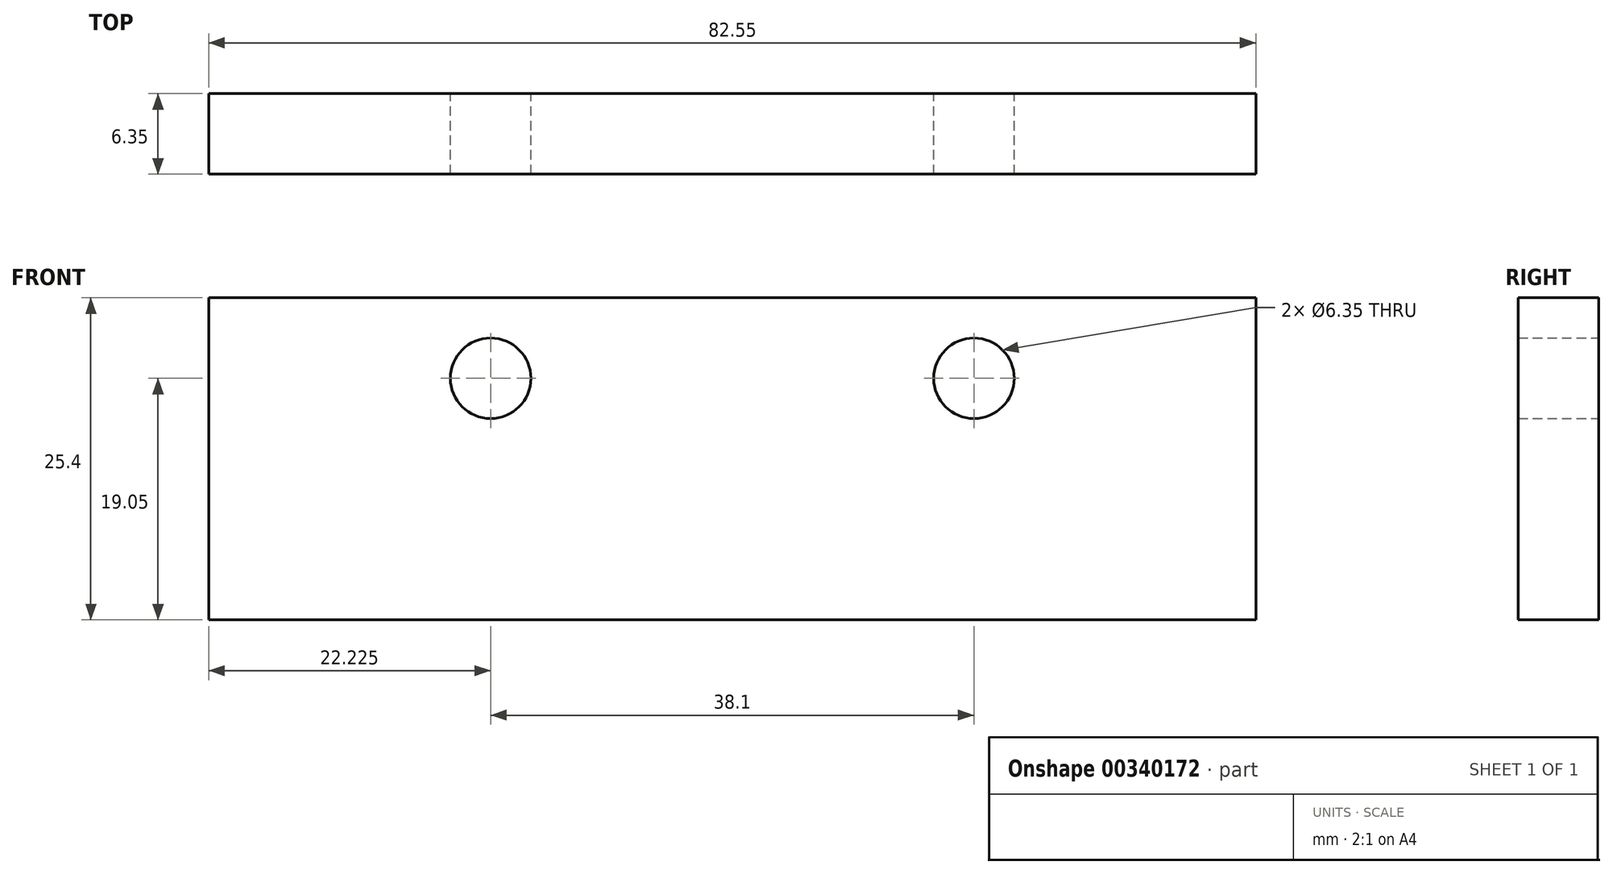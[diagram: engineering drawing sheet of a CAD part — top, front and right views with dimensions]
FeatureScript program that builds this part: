
annotation { "Feature Type Name" : "Feature", "Feature Type Description" : "" }
export const myFeature = defineFeature(function(context is Context, id is Id, definition is map)
    precondition{}
    {
        {
            var Q0;
            Q0=qCreatedBy(makeId("Front.planeOp"),FACE);
            var sketch = newSketch(context, id + "F0", { "sketchPlane" : qUnion([Q0])});
            skLineSegment(sketch, "E0.bottom", {"start": v(0, 0) * mm, "end": v(82.55, 0) * mm});
            skLineSegment(sketch, "E0.top", {"start": v(0, 25.4) * mm, "end": v(82.55, 25.4) * mm});
            skLineSegment(sketch, "E0.left", {"start": v(0, 0) * mm, "end": v(0, 25.4) * mm});
            skLineSegment(sketch, "E0.right", {"start": v(82.55, 0) * mm, "end": v(82.55, 25.4) * mm});
            skCircle(sketch, "E1", {"center": v(22.22, 19.05) * mm, "radius": 3.18 * mm});
            skCircle(sketch, "E2", {"center": v(60.33, 19.05) * mm, "radius": 3.18 * mm});
            skSolve(sketch);
        }
        {
            var Q0;
            Q0 = qSketchRegion(id + "F0", true);
            extrude(context, id + "F1", {"entities" : qUnion([Q0]), "depth" : 6.35 * mm});
        }
    });
